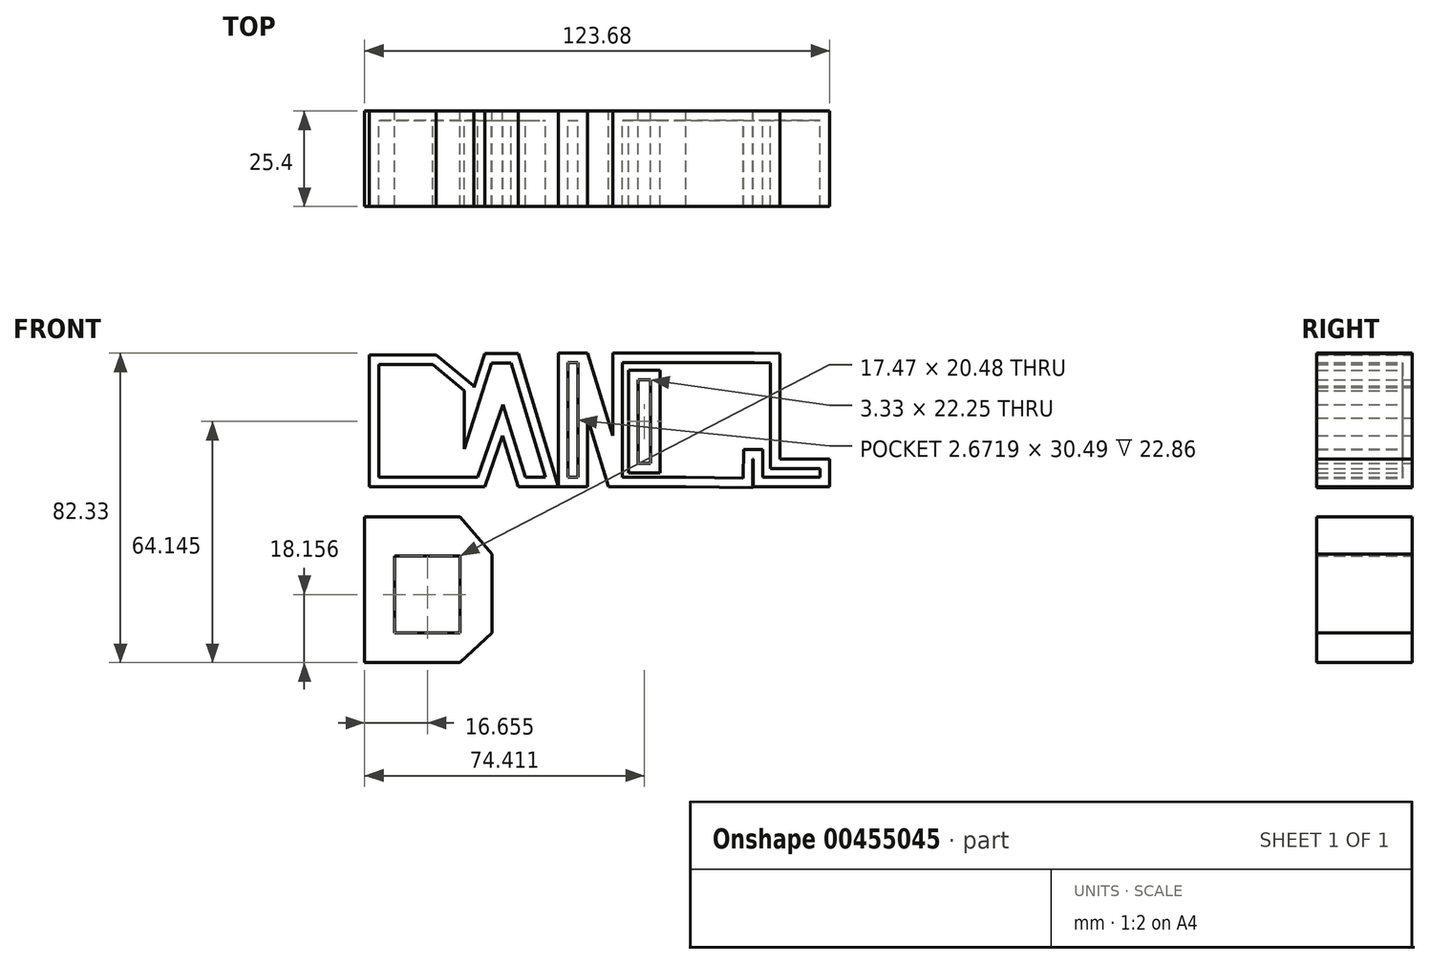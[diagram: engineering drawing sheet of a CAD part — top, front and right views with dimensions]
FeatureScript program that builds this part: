
annotation { "Feature Type Name" : "Feature", "Feature Type Description" : "" }
export const myFeature = defineFeature(function(context is Context, id is Id, definition is map)
    precondition{}
    {
        {
            var Q0;
            Q0=qCreatedBy(makeId("Front.planeOp"),FACE);
            var sketch = newSketch(context, id + "F0", { "sketchPlane" : qUnion([Q0])});
            skLineSegment(sketch, "E0", {"start": v(-38.6, 0) * mm, "end": v(-27.4, 35.43) * mm});
            skLineSegment(sketch, "E1", {"start": v(-27.4, 35.43) * mm, "end": v(-18.43, 35.43) * mm});
            skLineSegment(sketch, "E2", {"start": v(-18.43, 35.43) * mm, "end": v(-7.75, 0) * mm});
            skLineSegment(sketch, "E3", {"start": v(-27.4, 0) * mm, "end": v(-22.69, 13.69) * mm});
            skLineSegment(sketch, "E4", {"start": v(-22.69, 13.69) * mm, "end": v(-18.43, 0) * mm});
            skLineSegment(sketch, "E5", {"start": v(-7.75, 0) * mm, "end": v(-7.75, 35.57) * mm});
            skLineSegment(sketch, "E6", {"start": v(-7.75, 35.57) * mm, "end": v(0, 35.57) * mm});
            skLineSegment(sketch, "E7", {"start": v(0, 35.57) * mm, "end": v(6.63, 13.6) * mm});
            skLineSegment(sketch, "E8", {"start": v(6.63, 13.6) * mm, "end": v(6.63, 35.57) * mm});
            skLineSegment(sketch, "E9", {"start": v(6.63, 35.57) * mm, "end": v(13.43, 35.57) * mm});
            skLineSegment(sketch, "E10", {"start": v(13.43, 35.57) * mm, "end": v(13.43, 0) * mm});
            skLineSegment(sketch, "E11", {"start": v(13.43, 0) * mm, "end": v(5.53, 0) * mm});
            skLineSegment(sketch, "E12", {"start": v(5.53, 0) * mm, "end": v(0, 18.35) * mm});
            skLineSegment(sketch, "E13", {"start": v(0, 18.35) * mm, "end": v(0, 0) * mm});
            skLineSegment(sketch, "E14", {"start": v(0, 0) * mm, "end": v(-7.75, 0) * mm});
            skLineSegment(sketch, "E15", {"start": v(13.43, 35.57) * mm, "end": v(26.09, 35.57) * mm});
            skLineSegment(sketch, "E16", {"start": v(26.09, 35.57) * mm, "end": v(26.09, 6.26) * mm});
            skLineSegment(sketch, "E17", {"start": v(26.24, 28.66) * mm, "end": v(23.29, 28.66) * mm});
            skLineSegment(sketch, "E18", {"start": v(23.29, 28.2) * mm, "end": v(23.29, 5.95) * mm});
            skLineSegment(sketch, "E19", {"start": v(23.29, 5.95) * mm, "end": v(26.09, 5.95) * mm});
            skLineSegment(sketch, "E20", {"start": v(26.4, 6.1) * mm, "end": v(26.09, 0) * mm});
            skLineSegment(sketch, "E21", {"start": v(26.09, 0) * mm, "end": v(13.43, 0) * mm});
            skLineSegment(sketch, "E22", {"start": v(13.43, 5.95) * mm, "end": v(16.75, 5.95) * mm});
            skLineSegment(sketch, "E23", {"start": v(16.75, 5.8) * mm, "end": v(16.75, 5.95) * mm});
            skLineSegment(sketch, "E24", {"start": v(16.75, 6.26) * mm, "end": v(13.43, 6.26) * mm});
            skLineSegment(sketch, "E25", {"start": v(16.75, 6.26) * mm, "end": v(16.75, 28.5) * mm});
            skLineSegment(sketch, "E26", {"start": v(17.07, 28.5) * mm, "end": v(13.43, 28.5) * mm});
            skLineSegment(sketch, "E27", {"start": v(13.43, 28.5) * mm, "end": v(13.43, 35.57) * mm});
            skLineSegment(sketch, "E28", {"start": v(-27.4, 0) * mm, "end": v(-38.6, 0) * mm});
            skLineSegment(sketch, "E29", {"start": v(-18.43, 0) * mm, "end": v(-7.75, 0) * mm});
            skLineSegment(sketch, "E30", {"start": v(26.09, 35.57) * mm, "end": v(44.29, 35.57) * mm});
            skLineSegment(sketch, "E31", {"start": v(44.29, 35.57) * mm, "end": v(44.29, 28.66) * mm});
            skLineSegment(sketch, "E32", {"start": v(44.29, 28.66) * mm, "end": v(34.02, 28.66) * mm});
            skLineSegment(sketch, "E33", {"start": v(34.02, 28.66) * mm, "end": v(34.02, 20.92) * mm});
            skPoint(sketch, "E33.endSnap0", {"position": v(26.09, 20.92) * mm});
            skLineSegment(sketch, "E34", {"start": v(34.02, 20.92) * mm, "end": v(40.4, 20.92) * mm});
            skLineSegment(sketch, "E35", {"start": v(40.55, 20.73) * mm, "end": v(40.4, 13.26) * mm});
            skLineSegment(sketch, "E36", {"start": v(40.4, 13.26) * mm, "end": v(34.02, 13.26) * mm});
            skLineSegment(sketch, "E37", {"start": v(34.49, 13.42) * mm, "end": v(34.49, 7.35) * mm});
            skLineSegment(sketch, "E38", {"start": v(34.18, 7.35) * mm, "end": v(43.98, 7.35) * mm});
            skLineSegment(sketch, "E39", {"start": v(43.98, 7.35) * mm, "end": v(43.98, 0) * mm});
            skLineSegment(sketch, "E40", {"start": v(43.82, -0.27) * mm, "end": v(26.09, 0) * mm});
            skLineSegment(sketch, "E41", {"start": v(44.29, 35.57) * mm, "end": v(43.82, -0.27) * mm});
            skLineSegment(sketch, "E42", {"start": v(43.98, 0) * mm, "end": v(64.36, 0) * mm});
            skLineSegment(sketch, "E43", {"start": v(64.36, 0) * mm, "end": v(64.36, 7.35) * mm});
            skLineSegment(sketch, "E44", {"start": v(64.36, 7.35) * mm, "end": v(51.13, 7.35) * mm});
            skLineSegment(sketch, "E45", {"start": v(51.13, 7.35) * mm, "end": v(51.13, 35.5) * mm});
            skLineSegment(sketch, "E46", {"start": v(51.13, 35.5) * mm, "end": v(44.29, 35.57) * mm});
            skSolve(sketch);
        }
        {
            var Q0;
            Q0 = qSketchRegion(id + "F0", true);
            extrude(context, id + "F1", {"entities" : qUnion([Q0]), "depth" : 25.4 * mm});
        }
        {
            var Q0;
            Q0=qCreatedBy(makeId("Front.planeOp"),FACE);
            var sketch = newSketch(context, id + "F2", { "sketchPlane" : qUnion([Q0])});
            skLineSegment(sketch, "E47", {"start": v(-58.09, 0) * mm, "end": v(-58.09, 35.04) * mm});
            skLineSegment(sketch, "E48", {"start": v(-58.09, 35.04) * mm, "end": v(-40.34, 35.04) * mm});
            skLineSegment(sketch, "E49", {"start": v(-40.34, 35.04) * mm, "end": v(-30.23, 26.8) * mm});
            skLineSegment(sketch, "E50", {"start": v(-30.23, 26.8) * mm, "end": v(-30.23, 11.06) * mm});
            skLineSegment(sketch, "E51", {"start": v(-30.23, 11.06) * mm, "end": v(-38.47, 0) * mm});
            skLineSegment(sketch, "E52", {"start": v(-38.47, 0) * mm, "end": v(-58.09, 0) * mm});
            skSolve(sketch);
        }
        {
            var Q0;
            Q0=makeQuery(id+"F2.imprint","IMPRINT",FACE,{"disambiguationData":[TD([[makeQuery(id+"F2.imprint","IMPRINT",EDGE,{"derivedFrom":sQuery(id+"F2.wireOp",EDGE,"E47")}),-1.0]])]});
            extrude(context, id + "F3", {"entities" : qUnion([Q0]), "operationType" : NewBodyOperationType.ADD, "depth" : 25.4 * mm});
        }
        {
            var Q0;
            Q0=makeQuery(id+"F3.boolean.opBoolean","MERGE",FACE,{"derivedFrom":[makeQuery(id+"F1.opExtrude","CAP_FACE",FACE,{"disambiguationData":[OSD([sQuery(id+"F0.wireOp",EDGE,"E0"),sQuery(id+"F0.wireOp",EDGE,"E1"),sQuery(id+"F0.wireOp",EDGE,"E2"),sQuery(id+"F0.wireOp",EDGE,"E3"),sQuery(id+"F0.wireOp",EDGE,"E4"),sQuery(id+"F0.wireOp",EDGE,"E28"),sQuery(id+"F0.wireOp",EDGE,"E29")])],"isStart":false}),makeQuery(id+"F3.opExtrude","CAP_FACE",FACE,{"disambiguationData":[OSD([sQuery(id+"F2.wireOp",EDGE,"E47"),sQuery(id+"F2.wireOp",EDGE,"E48"),sQuery(id+"F2.wireOp",EDGE,"E49"),sQuery(id+"F2.wireOp",EDGE,"E50"),sQuery(id+"F2.wireOp",EDGE,"E51"),sQuery(id+"F2.wireOp",EDGE,"E52")])],"isStart":false})]});
            shell(context, id + "F4", {"entities" : qUnion([Q0]), "thickness" : 2.54 * mm});
        }
        {
            var Q0;
            Q0=makeQuery(id+"F1.opExtrude","CAP_FACE",FACE,{"disambiguationData":[OSD([sQuery(id+"F0.wireOp",EDGE,"E5"),sQuery(id+"F0.wireOp",EDGE,"E6"),sQuery(id+"F0.wireOp",EDGE,"E7"),sQuery(id+"F0.wireOp",EDGE,"E8"),sQuery(id+"F0.wireOp",EDGE,"E9"),sQuery(id+"F0.wireOp",EDGE,"E10"),sQuery(id+"F0.wireOp",EDGE,"E11"),sQuery(id+"F0.wireOp",EDGE,"E12"),sQuery(id+"F0.wireOp",EDGE,"E13"),sQuery(id+"F0.wireOp",EDGE,"E14"),sQuery(id+"F0.wireOp",EDGE,"E15"),sQuery(id+"F0.wireOp",EDGE,"E21"),sQuery(id+"F0.wireOp",EDGE,"E24"),sQuery(id+"F0.wireOp",EDGE,"E25"),sQuery(id+"F0.wireOp",EDGE,"E26"),sQuery(id+"F0.wireOp",EDGE,"E30"),sQuery(id+"F0.wireOp",EDGE,"E38"),sQuery(id+"F0.wireOp",EDGE,"E39"),sQuery(id+"F0.wireOp",EDGE,"E40"),sQuery(id+"F0.wireOp",EDGE,"E41"),sQuery(id+"F0.wireOp",EDGE,"E42"),sQuery(id+"F0.wireOp",EDGE,"E43"),sQuery(id+"F0.wireOp",EDGE,"E44"),sQuery(id+"F0.wireOp",EDGE,"E45"),sQuery(id+"F0.wireOp",EDGE,"E46")])],"isStart":false});
            shell(context, id + "F5", {"entities" : qUnion([Q0]), "thickness" : 2.54 * mm});
        }
        {
            var Q0;
            Q0=qCreatedBy(makeId("Front.planeOp"),FACE);
            var sketch = newSketch(context, id + "F6", { "sketchPlane" : qUnion([Q0])});
            skLineSegment(sketch, "E53", {"start": v(-59.32, -7.99) * mm, "end": v(-59.32, -46.76) * mm});
            skLineSegment(sketch, "E54", {"start": v(-59.32, -46.76) * mm, "end": v(-33.93, -46.76) * mm});
            skLineSegment(sketch, "E55", {"start": v(-33.93, -46.76) * mm, "end": v(-25.46, -38.84) * mm});
            skLineSegment(sketch, "E56", {"start": v(-25.46, -38.84) * mm, "end": v(-25.46, -17.82) * mm});
            skLineSegment(sketch, "E57", {"start": v(-25.46, -17.82) * mm, "end": v(-33.93, -7.99) * mm});
            skLineSegment(sketch, "E58", {"start": v(-33.93, -7.99) * mm, "end": v(-59.32, -7.99) * mm});
            skLineSegment(sketch, "E59", {"start": v(-51.4, -18.37) * mm, "end": v(-51.4, -38.84) * mm});
            skLineSegment(sketch, "E60", {"start": v(-51.4, -38.84) * mm, "end": v(-33.93, -38.84) * mm});
            skLineSegment(sketch, "E61", {"start": v(-33.93, -38.84) * mm, "end": v(-33.93, -18.37) * mm});
            skLineSegment(sketch, "E62", {"start": v(-33.93, -18.37) * mm, "end": v(-51.4, -18.37) * mm});
            skSolve(sketch);
        }
        {
            var Q0;
            Q0=makeQuery(id+"F6.imprint","IMPRINT",FACE,{"disambiguationData":[TD([[makeQuery(id+"F6.imprint","IMPRINT",EDGE,{"derivedFrom":sQuery(id+"F6.wireOp",EDGE,"E53")}),1.0]])]});
            extrude(context, id + "F7", {"entities" : qUnion([Q0]), "depth" : 25.4 * mm});
        }
    });
